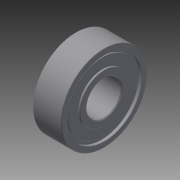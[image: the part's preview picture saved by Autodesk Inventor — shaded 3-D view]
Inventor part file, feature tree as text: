
AUTODESK INVENTOR PART (.ipt)
format: ipt  version: 2015 (Build 190159000, 159)  size: 188,928 bytes
history: native  units: mm
features: fillet x3, chamfer x2, sketch x2, revolve x1, extrude x1
ambient origin geometry x8: Origin, YZ Plane, XZ Plane, XY Plane, X Axis, Y Axis, Z Axis, Center Point
bodies: Solid1 (feature_tree)
feature tree (9):
  revolve  "Revolution1"  [1 undecoded]
  extrude  "Extrusion1"  Depth=0.2mm
  chamfer  "Chamfer1"  Distance=1.0mm
  chamfer  "Chamfer2"  Distance=2.5mm
  fillet  "Fillet1"  Radius=7.5mm
  fillet  "Fillet2"  [1 undecoded]
  fillet  "Fillet3"  Radius=6.0mm
  sketch  "Sketch1"  dims[d2=4.25mm d3=0.3mm]
  sketch  "Sketch2"  dims[d4=1.8mm d5=0.2mm d6=1.0mm d8=2.5mm d9=7.5mm d10=90.0deg d11=6.0mm d12=5.0mm d13=0.0mm d14=0.15mm d15=2.0mm d16=45.0deg d17=0.15mm d18=2.0mm d19=45.0deg d20=0.15mm d21=0.15mm d22=0.15mm]
note: 2 required parameter values undecoded (feature->parameter linkage not recoverable at this tier; creation-order binding heuristic only, values carry confidence <= 0.55)